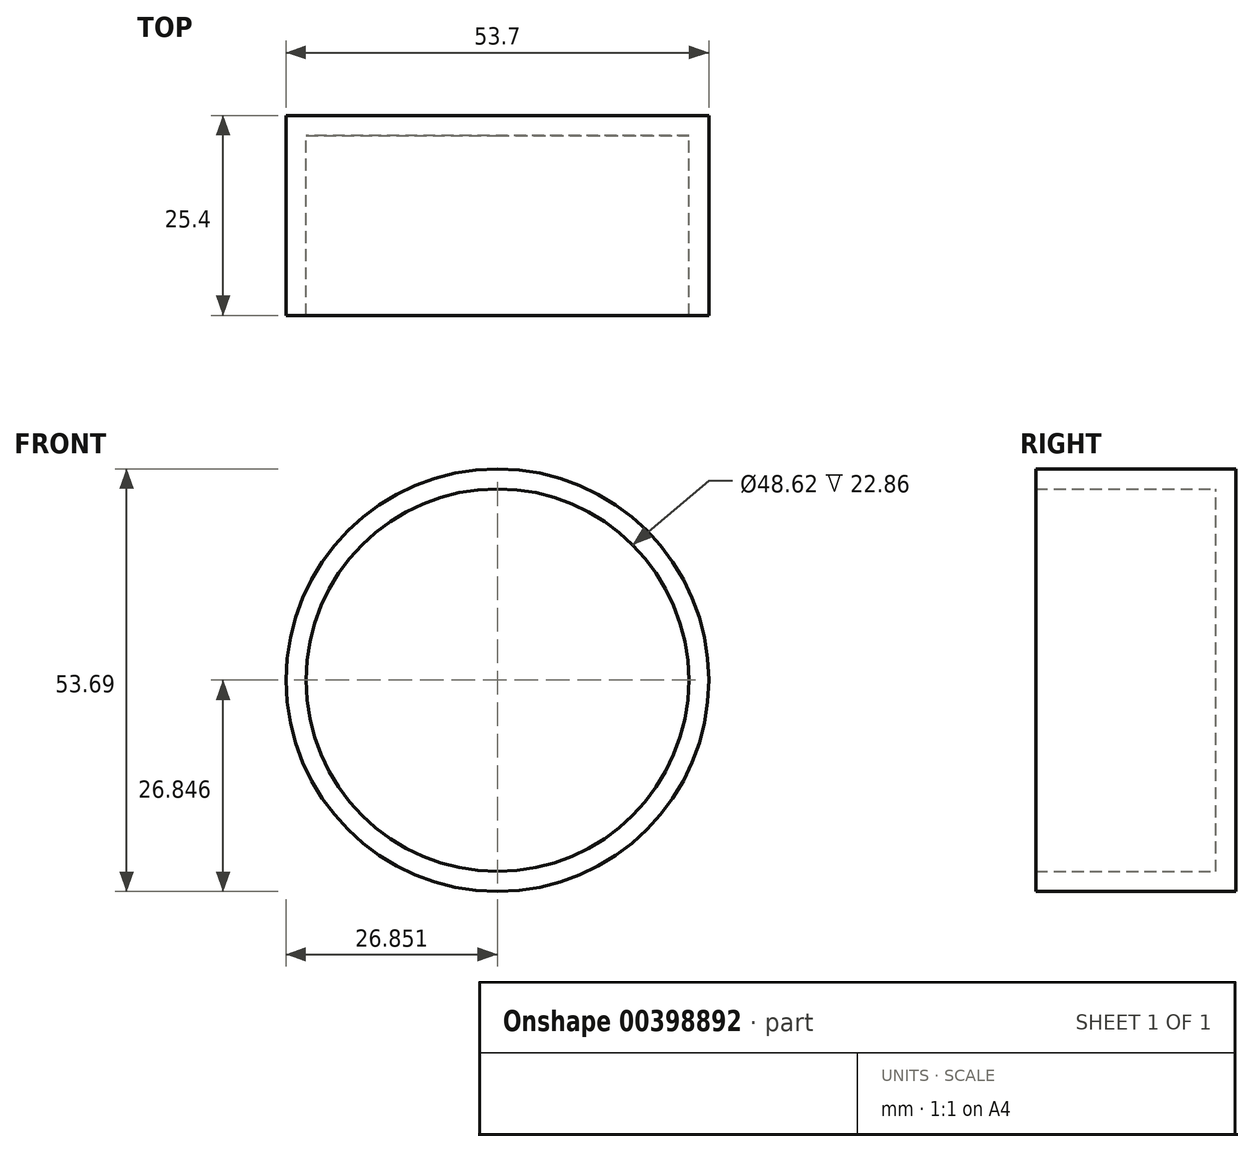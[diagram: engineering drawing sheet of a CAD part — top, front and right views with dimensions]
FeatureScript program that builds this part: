
annotation { "Feature Type Name" : "Feature", "Feature Type Description" : "" }
export const myFeature = defineFeature(function(context is Context, id is Id, definition is map)
    precondition{}
    {
        {
            var Q0;
            Q0=qCreatedBy(makeId("Front.planeOp"),FACE);
            var sketch = newSketch(context, id + "F0", { "sketchPlane" : qUnion([Q0])});
            skCircle(sketch, "E0", {"center": v(-42.3, 19.87) * mm, "radius": 26.85 * mm});
            skCircle(sketch, "E1", {"center": v(-23.62, 0.58) * mm, "radius": 26.8 * mm});
            skSolve(sketch);
        }
        {
            var Q0;
            {var subQ0=sQuery(id+"F0.wireOp",EDGE,"E1");var subQ1=sQuery(id+"F0.wireOp",EDGE,"E0");var subQ2=makeQuery(id+"F0.imprint","INTERSECT",VERTEX,{"disambiguationData":[OD(0.0)],"derivedFrom":[subQ1,subQ0]});Q0=makeQuery(id+"F0.imprint","IMPRINT",FACE,{"disambiguationData":[TD([[makeQuery(id+"F0.imprint","IMPRINT",EDGE,{"disambiguationData":[TD([[subQ2,1.0]])],"derivedFrom":subQ1}),1.0]])]});}
            var Q1;
            {var subQ0=sQuery(id+"F0.wireOp",EDGE,"E1");var subQ1=sQuery(id+"F0.wireOp",EDGE,"E0");var subQ2=makeQuery(id+"F0.imprint","INTERSECT",VERTEX,{"disambiguationData":[OD(0.0)],"derivedFrom":[subQ1,subQ0]});Q1=makeQuery(id+"F0.imprint","IMPRINT",FACE,{"disambiguationData":[TD([[makeQuery(id+"F0.imprint","IMPRINT",EDGE,{"disambiguationData":[TD([[subQ2,-1.0]])],"derivedFrom":subQ1}),1.0]])]});}
            extrude(context, id + "F1", {"entities" : qUnion([Q0, Q1]), "depth" : 25.4 * mm});
        }
        {
            var Q0;
            Q0=makeQuery(id+"F1.opExtrude","CAP_FACE",FACE,{"disambiguationData":[OSD([sQuery(id+"F0.wireOp",EDGE,"E0")])],"isStart":false});
            shell(context, id + "F2", {"entities" : qUnion([Q0]), "thickness" : 2.54 * mm});
        }
    });
